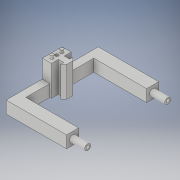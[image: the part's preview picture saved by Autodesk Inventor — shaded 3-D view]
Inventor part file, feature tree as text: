
AUTODESK INVENTOR PART (.ipt)
format: ipt  version: 2018 (Build 220112000, 112)  size: 195,072 bytes
history: native  units: in
note: dims shown in document units (in); Inventor stores cm internally (conversion verified against a paired STEP export)
features: sketch x11, extrude x8, hole x3
ambient origin geometry x8: Origin, YZ Plane, XZ Plane, XY Plane, X Axis, Y Axis, Z Axis, Center Point
bodies: Solid1 (feature_tree)
feature tree (22):
  extrude  "Extrusion1"  Depth=0.65in
  extrude  "Extrusion2"  Depth=0.28in
  hole  "Hole1"  [1 undecoded]
  extrude  "Extrusion3"  Depth=0.1in
  extrude  "Extrusion4"  Depth=1.0in
  extrude  "Extrusion5"  Depth=0.11in
  hole  "Hole2"  [1 undecoded]
  extrude  "Extrusion6"  Depth=0.25in
  extrude  "Extrusion7"  Depth=1.2in TaperAngle=0.0deg
  extrude  "Extrusion8"  Depth=1.75in TaperAngle=0.0deg
  hole  "Hole3"  [1 undecoded]
  sketch  "Sketch1"  dims[d0=0.3in d1=0.65in]
  sketch  "Sketch2"  dims[d2=0.225in d3=0.28in]
  sketch  "Sketch3"  dims[d4=0.2in d5=0.1in]
  sketch  "Sketch4"  dims[d6=0.1in d7=0.1in]
  sketch  "Sketch5"  dims[d8=1.0in d9=0.0in d10=0.16in]
  sketch  "Sketch6"  dims[d11=0.16in d12=0.11in]
  sketch  "Sketch7"  dims[d13=0.11in d14=0.1in d15=0.0in]
  sketch  "Sketch8"  dims[d16=0.325in]
  sketch  "Sketch9"  dims[d17=0.11in d18=0.75in d19=0.375in d20=0.25in d21=0.5635in d22=0.45in d23=0.8108in d24=0.25in]
  sketch  "Sketch10"  dims[d25=0.4in d26=1.2in d27=0.0in]
  sketch  "Sketch11"  dims[d28=0.4in d29=1.75in d30=0.0in d31=0.2in d32=0.2in d33=0.5in d34=0.0in d35=0.11in d36=0.11in d37=0.75in d38=0.375in d39=0.25in d40=0.5635in d41=0.63in d42=0.8108in d43=0.25in d44=0.4in d45=1.2in d46=0.0in d47=0.4in d48=1.75in d49=0.0in d50=0.2in d51=0.2in d52=0.5in d53=0.0in d54=0.11in d55=0.11in d56=0.75in d57=0.375in d58=0.25in d59=0.5635in d60=0.63in d61=0.8108in]
note: 3 required parameter values undecoded (feature->parameter linkage not recoverable at this tier; creation-order binding heuristic only, values carry confidence <= 0.55)
